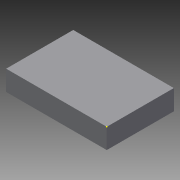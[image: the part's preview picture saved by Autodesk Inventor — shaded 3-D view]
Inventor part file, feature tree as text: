
AUTODESK INVENTOR PART (.ipt)
format: ipt  version: 2015 (Build 190159000, 159)  size: 70,144 bytes
history: native  units: in
note: dims shown in document units (in); Inventor stores cm internally (conversion verified against a paired STEP export)
features: sketch x3, extrude x1
ambient origin geometry x8: Origin, YZ Plane, XZ Plane, XY Plane, X Axis, Y Axis, Z Axis, Center Point
bodies: Solid1 (feature_tree)
feature tree (4):
  extrude  "Extrusion1"  Depth=10.0in
  sketch  "Sketch2"  dims[d2=3.0in d3=0.0in]
  sketch  "Sketch3"
  sketch  "Sketch1"  dims[d0=15.0in d1=10.0in]
